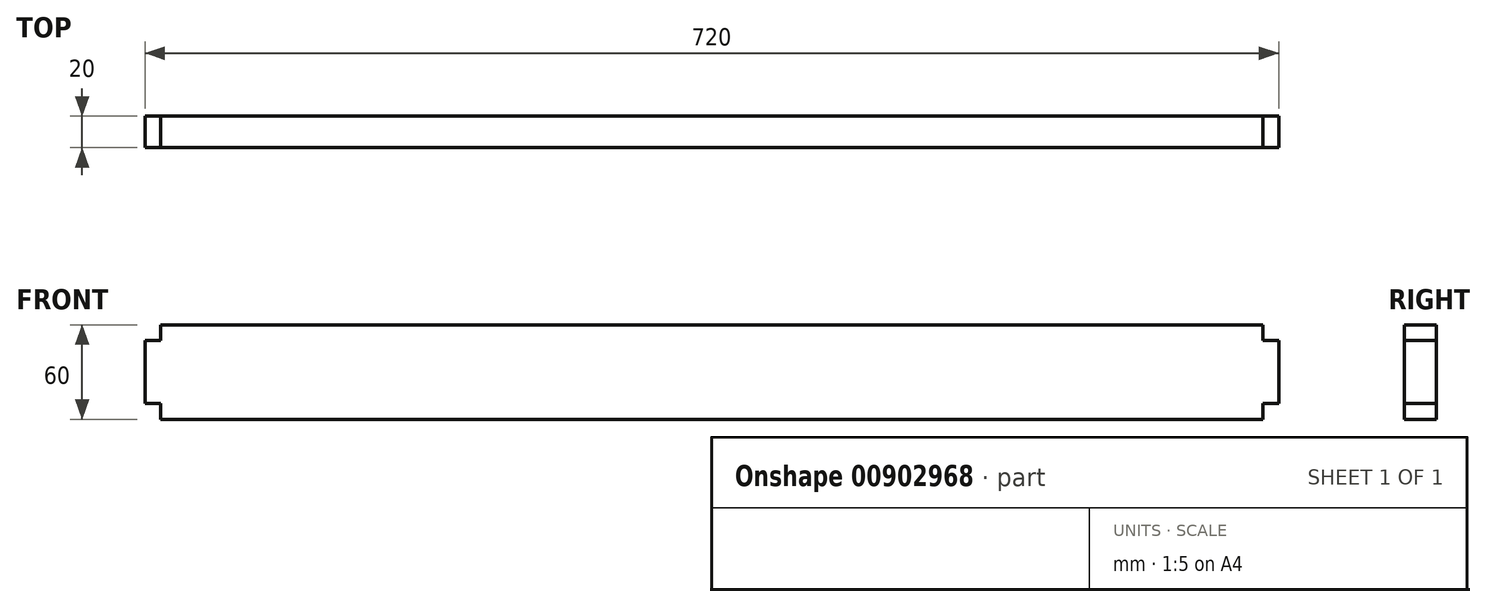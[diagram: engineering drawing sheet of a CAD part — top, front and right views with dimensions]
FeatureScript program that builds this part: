
annotation { "Feature Type Name" : "Feature", "Feature Type Description" : "" }
export const myFeature = defineFeature(function(context is Context, id is Id, definition is map)
    precondition{}
    {
        {
            var Q0;
            Q0=qCreatedBy(makeId("Right.planeOp"),FACE);
            var sketch = newSketch(context, id + "F0", { "sketchPlane" : qUnion([Q0])});
            skLineSegment(sketch, "E0.bottom", {"start": v(0, 0) * mm, "end": v(20, 0) * mm});
            skLineSegment(sketch, "E0.top", {"start": v(0, -60) * mm, "end": v(20, -60) * mm});
            skLineSegment(sketch, "E0.left", {"start": v(0, 0) * mm, "end": v(0, -60) * mm});
            skLineSegment(sketch, "E0.right", {"start": v(20, 0) * mm, "end": v(20, -60) * mm});
            skSolve(sketch);
        }
        {
            var Q0;
            Q0=qSketchRegion(id+"F0",true);
            extrude(context, id + "F1", {"entities" : qUnion([Q0]), "depth" : 700 * mm, "offsetDistance" : 25 * mm});
        }
        {
            var Q0;
            Q0=makeQuery(id+"F1.opExtrude","CAP_FACE",FACE,{"disambiguationData":[OSD([sQuery(id+"F0.wireOp",EDGE,"E0.bottom"),sQuery(id+"F0.wireOp",EDGE,"E0.top"),sQuery(id+"F0.wireOp",EDGE,"E0.left"),sQuery(id+"F0.wireOp",EDGE,"E0.right")])],"isStart":true});
            var sketch = newSketch(context, id + "F2", { "sketchPlane" : qUnion([Q0])});
            skLineSegment(sketch, "E1.bottom", {"start": v(-20, -10) * mm, "end": v(0, -10) * mm});
            skLineSegment(sketch, "E1.top", {"start": v(-20, -50) * mm, "end": v(0, -50) * mm});
            skLineSegment(sketch, "E1.left", {"start": v(-20, -10) * mm, "end": v(-20, -50) * mm});
            skLineSegment(sketch, "E1.right", {"start": v(0, -10) * mm, "end": v(0, -50) * mm});
            skSolve(sketch);
        }
        {
            var Q0;
            Q0 = qSketchRegion(id + "F2", true);
            extrude(context, id + "F3", {"entities" : qUnion([Q0]), "operationType" : NewBodyOperationType.ADD, "depth" : 10 * mm, "offsetDistance" : 25 * mm});
        }
        {
            var Q0;
            Q0=makeQuery(id+"F1.opExtrude","CAP_FACE",FACE,{"disambiguationData":[OSD([sQuery(id+"F0.wireOp",EDGE,"E0.bottom"),sQuery(id+"F0.wireOp",EDGE,"E0.top"),sQuery(id+"F0.wireOp",EDGE,"E0.left"),sQuery(id+"F0.wireOp",EDGE,"E0.right")])],"isStart":false});
            var sketch = newSketch(context, id + "F4", { "sketchPlane" : qUnion([Q0])});
            skLineSegment(sketch, "E2.bottom", {"start": v(20, -10) * mm, "end": v(0, -10) * mm});
            skLineSegment(sketch, "E2.top", {"start": v(20, -50) * mm, "end": v(0, -50) * mm});
            skLineSegment(sketch, "E2.left", {"start": v(20, -10) * mm, "end": v(20, -50) * mm});
            skLineSegment(sketch, "E2.right", {"start": v(0, -10) * mm, "end": v(0, -50) * mm});
            skSolve(sketch);
        }
        {
            var Q0;
            Q0 = qSketchRegion(id + "F4", true);
            extrude(context, id + "F5", {"entities" : qUnion([Q0]), "operationType" : NewBodyOperationType.ADD, "depth" : 10 * mm, "offsetDistance" : 25 * mm});
        }
    });
